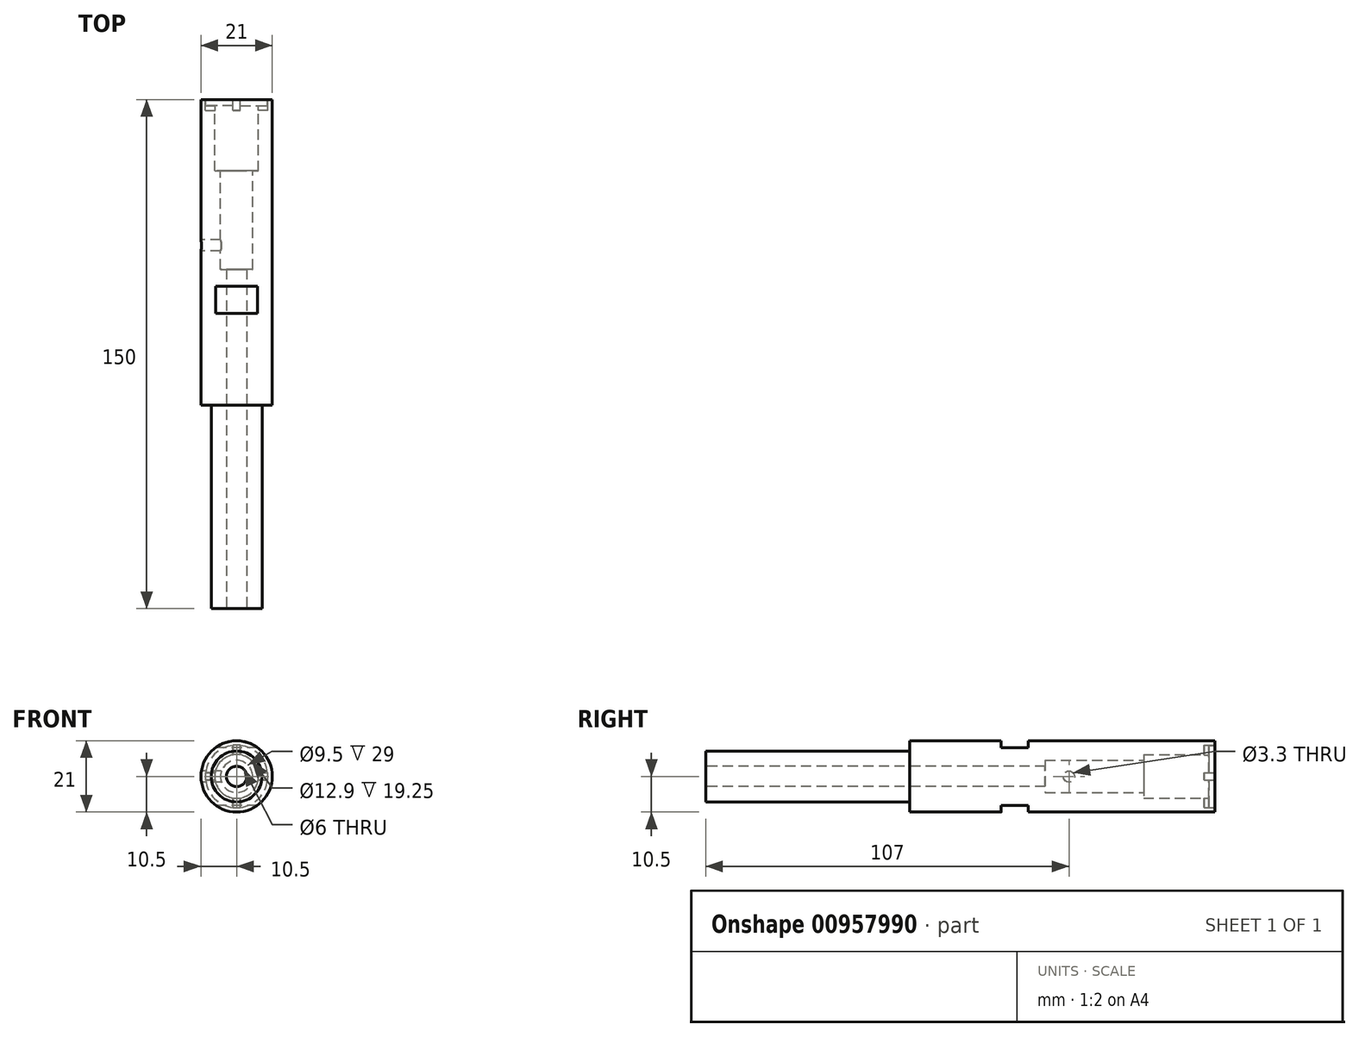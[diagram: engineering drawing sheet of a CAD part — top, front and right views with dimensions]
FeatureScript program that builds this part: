
annotation { "Feature Type Name" : "Feature", "Feature Type Description" : "" }
export const myFeature = defineFeature(function(context is Context, id is Id, definition is map)
    precondition{}
    {
        {
            var Q0;
            Q0=qCreatedBy(makeId("Front.planeOp"),FACE);
            var sketch = newSketch(context, id + "F0", { "sketchPlane" : qUnion([Q0])});
            skCircle(sketch, "E0", {"center": v(0, 0) * mm, "radius": 10.5 * mm});
            skSolve(sketch);
        }
        {
            var Q0;
            Q0=makeQuery(id+"F0.imprint","IMPRINT",FACE,{"disambiguationData":[TD([[makeQuery(id+"F0.imprint","IMPRINT",EDGE,{"derivedFrom":sQuery(id+"F0.wireOp",EDGE,"E0")}),1.0]])]});
            extrude(context, id + "F1", {"entities" : qUnion([Q0]), "depth" : 90 * mm, "offsetDistance" : 25 * mm});
        }
        {
            var Q0;
            Q0=makeQuery(id+"F1.opExtrude","CAP_FACE",FACE,{"disambiguationData":[OSD([sQuery(id+"F0.wireOp",EDGE,"E0")])],"isStart":false});
            var sketch = newSketch(context, id + "F2", { "sketchPlane" : qUnion([Q0])});
            skCircle(sketch, "E1", {"center": v(0, 0) * mm, "radius": 7.5 * mm});
            skSolve(sketch);
        }
        {
            var Q0;
            Q0=makeQuery(id+"F2.imprint","IMPRINT",FACE,{"disambiguationData":[TD([[makeQuery(id+"F2.imprint","IMPRINT",EDGE,{"derivedFrom":sQuery(id+"F2.wireOp",EDGE,"E1")}),1.0]])]});
            extrude(context, id + "F3", {"entities" : qUnion([Q0]), "operationType" : NewBodyOperationType.ADD, "depth" : 60 * mm, "offsetDistance" : 25 * mm});
        }
        {
            var Q0;
            Q0=makeQuery(id+"F3.opExtrude","CAP_FACE",FACE,{"disambiguationData":[OSD([sQuery(id+"F2.wireOp",EDGE,"E1")])],"isStart":false});
            var sketch = newSketch(context, id + "F4", { "sketchPlane" : qUnion([Q0])});
            skPoint(sketch, "E2", {"position": v(0, 0) * mm});
            skSolve(sketch);
        }
        {
            var Q0;
            Q0=sQuery(id+"F4.wireOp",VERTEX,"E2");
            var Q1;
            Q1=makeQuery(id+"F1.opExtrude","SWEPT_BODY",BODY,{"disambiguationData":[OSD([sQuery(id+"F0.wireOp",EDGE,"E0")])]});
            hole(context, id + "F5", {"style" : HoleStyle.SIMPLE, "endStyle" : HoleEndStyle.THROUGH, "standardTappedOrClearance" : lookupTablePath({ "standard" : "ISO", "size" : "6", "type" : "Drilled" }), "standardBlindInLast" : lookupTablePath({ "standard" : "ISO", "size" : "6", "type" : "Drilled" }), "holeDiameter" : 6 * mm, "majorDiameter" : 5 * mm, "isTappedThrough" : true, "tappedDepth" : 11.5 * mm, "tapClearance" : 3, "startFromSketch" : true, "locations" : qUnion([Q0]), "scope" : qUnion([Q1])});
        }
        {
            var Q0;
            Q0=makeQuery(id+"F1.opExtrude","CAP_FACE",FACE,{"disambiguationData":[OSD([sQuery(id+"F0.wireOp",EDGE,"E0")])],"isStart":true});
            var sketch = newSketch(context, id + "F6", { "sketchPlane" : qUnion([Q0])});
            skCircle(sketch, "E3", {"center": v(0, 0) * mm, "radius": 4.75 * mm});
            skSolve(sketch);
        }
        {
            var Q0;
            Q0=makeQuery(id+"F6.imprint","IMPRINT",FACE,{"disambiguationData":[TD([[makeQuery(id+"F6.imprint","IMPRINT",EDGE,{"derivedFrom":sQuery(id+"F6.wireOp",EDGE,"E3")}),1.0]])]});
            extrude(context, id + "F7", {"entities" : qUnion([Q0]), "operationType" : NewBodyOperationType.REMOVE, "oppositeDirection" : true, "depth" : 50 * mm, "offsetDistance" : 25 * mm});
        }
        {
            var Q0;
            Q0=makeQuery(id+"F1.opExtrude","CAP_FACE",FACE,{"disambiguationData":[OSD([sQuery(id+"F0.wireOp",EDGE,"E0")])],"isStart":true});
            var sketch = newSketch(context, id + "F8", { "sketchPlane" : qUnion([Q0])});
            skCircle(sketch, "E4", {"center": v(0, 0) * mm, "radius": 6.45 * mm});
            skSolve(sketch);
        }
        {
            var Q0;
            Q0 = qSketchRegion(id + "F8", true);
            extrude(context, id + "F9", {"entities" : qUnion([Q0]), "operationType" : NewBodyOperationType.REMOVE, "oppositeDirection" : true, "depth" : 21 * mm, "offsetDistance" : 25 * mm});
        }
        {
            var Q0;
            Q0=qCreatedBy(makeId("Front.planeOp"),FACE);
            var sketch = newSketch(context, id + "F10", { "sketchPlane" : qUnion([Q0])});
            skCircle(sketch, "E5", {"center": v(0, 0) * mm, "radius": 9.2 * mm});
            skSolve(sketch);
        }
        {
            var Q0;
            Q0 = qSketchRegion(id + "F10", true);
            extrude(context, id + "F11", {"entities" : qUnion([Q0]), "operationType" : NewBodyOperationType.REMOVE, "depth" : 1.75 * mm, "offsetDistance" : 25 * mm});
        }
        {
            var Q0;
            Q0=qCreatedBy(makeId("Front.planeOp"),FACE);
            var sketch = newSketch(context, id + "F12", { "sketchPlane" : qUnion([Q0])});
            skPoint(sketch, "E6", {"position": v(1.1, 0) * mm});
            skPoint(sketch, "E7", {"position": v(-1.1, 0) * mm});
            skPoint(sketch, "E8", {"position": v(0, 1.1) * mm});
            skPoint(sketch, "E9", {"position": v(0, -1.1) * mm});
            skLineSegment(sketch, "E10", {"start": v(1.1, 0) * mm, "end": v(1.1, 9.2) * mm});
            skLineSegment(sketch, "E11", {"start": v(1.1, 9.2) * mm, "end": v(-1.1, 9.2) * mm});
            skLineSegment(sketch, "E12", {"start": v(-1.1, 9.2) * mm, "end": v(-1.1, -9.2) * mm});
            skLineSegment(sketch, "E13", {"start": v(-1.1, -9.2) * mm, "end": v(1.1, -9.2) * mm});
            skLineSegment(sketch, "E14", {"start": v(1.1, -9.2) * mm, "end": v(1.1, 0) * mm});
            skLineSegment(sketch, "E15", {"start": v(0, 1.1) * mm, "end": v(-9.2, 1.1) * mm});
            skLineSegment(sketch, "E16", {"start": v(-9.2, 1.1) * mm, "end": v(-9.2, -1.1) * mm});
            skLineSegment(sketch, "E17", {"start": v(-9.2, -1.1) * mm, "end": v(0, -1.1) * mm});
            skLineSegment(sketch, "E18", {"start": v(9.2, -1.1) * mm, "end": v(9.2, 1.1) * mm});
            skLineSegment(sketch, "E19", {"start": v(9.2, 1.1) * mm, "end": v(0, 1.1) * mm});
            skLineSegment(sketch, "E20", {"start": v(9.2, -1.1) * mm, "end": v(0, -1.1) * mm});
            skSolve(sketch);
        }
        {
            var Q0;
            Q0 = qSketchRegion(id + "F12", true);
            extrude(context, id + "F13", {"entities" : qUnion([Q0]), "operationType" : NewBodyOperationType.REMOVE, "depth" : 3.25 * mm, "offsetDistance" : 25 * mm});
        }
        {
            var Q0;
            Q0=qCreatedBy(makeId("Top.planeOp"),FACE);
            cPlane(context, id + "F14", {"entities" : qUnion([Q0]), "cplaneType" : CPlaneType.OFFSET, "offset" : 10.5 * mm, "width" : 150 * mm, "height" : 150 * mm});
        }
        {
            var Q0;
            Q0=qCreatedBy(id+"F14.planeOp",FACE);
            var sketch = newSketch(context, id + "F15", { "sketchPlane" : qUnion([Q0])});
            skPoint(sketch, "E21", {"position": v(21.83, -55) * mm});
            skPoint(sketch, "E22", {"position": v(-27.22, -55) * mm});
            skPoint(sketch, "E23", {"position": v(-27.22, -63) * mm});
            skPoint(sketch, "E24", {"position": v(21.83, -63) * mm});
            skLineSegment(sketch, "E25", {"start": v(21.83, -55) * mm, "end": v(21.83, -63) * mm});
            skLineSegment(sketch, "E26", {"start": v(-27.22, -63) * mm, "end": v(-27.22, -55) * mm});
            skLineSegment(sketch, "E27", {"start": v(21.83, -55) * mm, "end": v(-27.22, -55) * mm});
            skLineSegment(sketch, "E28", {"start": v(-27.22, -63) * mm, "end": v(21.83, -63) * mm});
            skSolve(sketch);
        }
        {
            var Q0;
            Q0=makeQuery(id+"F15.imprint","IMPRINT",FACE,{"disambiguationData":[TD([[makeQuery(id+"F15.imprint","IMPRINT",EDGE,{"derivedFrom":sQuery(id+"F15.wireOp",EDGE,"E25")}),-1.0]])]});
            extrude(context, id + "F16", {"entities" : qUnion([Q0]), "operationType" : NewBodyOperationType.REMOVE, "oppositeDirection" : true, "depth" : 2 * mm, "offsetDistance" : 25 * mm});
        }
        {
            var Q0;
            Q0=qCreatedBy(makeId("Top.planeOp"),FACE);
            cPlane(context, id + "F17", {"entities" : qUnion([Q0]), "cplaneType" : CPlaneType.OFFSET, "offset" : 10.5 * mm, "oppositeDirection" : true, "width" : 150 * mm, "height" : 150 * mm});
        }
        {
            var Q0;
            Q0=qCreatedBy(id+"F17.planeOp",FACE);
            var sketch = newSketch(context, id + "F18", { "sketchPlane" : qUnion([Q0])});
            skPoint(sketch, "E29", {"position": v(20.46, -55) * mm});
            skPoint(sketch, "E30", {"position": v(-19.3, -55) * mm});
            skPoint(sketch, "E31", {"position": v(-19.3, -63) * mm});
            skPoint(sketch, "E32", {"position": v(20.46, -63) * mm});
            skLineSegment(sketch, "E33", {"start": v(20.46, -55) * mm, "end": v(-19.3, -55) * mm});
            skLineSegment(sketch, "E34", {"start": v(-19.3, -55) * mm, "end": v(-19.3, -63) * mm});
            skLineSegment(sketch, "E35", {"start": v(-19.3, -63) * mm, "end": v(20.46, -63) * mm});
            skLineSegment(sketch, "E36", {"start": v(20.46, -63) * mm, "end": v(20.46, -55) * mm});
            skSolve(sketch);
        }
        {
            var Q0;
            Q0=makeQuery(id+"F18.imprint","IMPRINT",FACE,{"disambiguationData":[TD([[makeQuery(id+"F18.imprint","IMPRINT",EDGE,{"derivedFrom":sQuery(id+"F18.wireOp",EDGE,"E33")}),1.0]])]});
            extrude(context, id + "F19", {"entities" : qUnion([Q0]), "operationType" : NewBodyOperationType.REMOVE, "depth" : 2 * mm, "offsetDistance" : 25 * mm});
        }
        {
            var Q0;
            Q0=qCreatedBy(makeId("Right.planeOp"),FACE);
            cPlane(context, id + "F20", {"entities" : qUnion([Q0]), "cplaneType" : CPlaneType.OFFSET, "offset" : 10.5 * mm, "oppositeDirection" : true, "width" : 150 * mm, "height" : 150 * mm});
        }
        {
            var Q0;
            Q0=qCreatedBy(id+"F20.planeOp",FACE);
            var sketch = newSketch(context, id + "F21", { "sketchPlane" : qUnion([Q0])});
            skPoint(sketch, "E37", {"position": v(-43, 0) * mm});
            skSolve(sketch);
        }
        {
            var Q0;
            Q0=sQuery(id+"F21.wireOp",VERTEX,"E37");
            var Q1;
            Q1=makeQuery(id+"F1.opExtrude","SWEPT_BODY",BODY,{"disambiguationData":[OSD([sQuery(id+"F0.wireOp",EDGE,"E0")])]});
            hole(context, id + "F22", {"style" : HoleStyle.SIMPLE, "endStyle" : HoleEndStyle.BLIND, "oppositeDirection" : true, "standardTappedOrClearance" : lookupTablePath({ "standard" : "ISO", "engagement" : "75%", "pitch" : "0.7 mm", "size" : "M4", "type" : "Tapped" }), "standardBlindInLast" : lookupTablePath({ "standard" : "ISO", "fit" : "Normal", "engagement" : "75%", "pitch" : "0.7 mm", "size" : "M4", "type" : "Clearance & tapped" }), "holeDiameter" : 3.3 * mm, "majorDiameter" : 4 * mm, "showTappedDepth" : true, "holeDepth" : 10 * mm, "isTappedThrough" : true, "tappedDepth" : 7.9 * mm, "tapClearance" : 3, "startFromSketch" : true, "locations" : qUnion([Q0]), "scope" : qUnion([Q1])});
        }
    });
